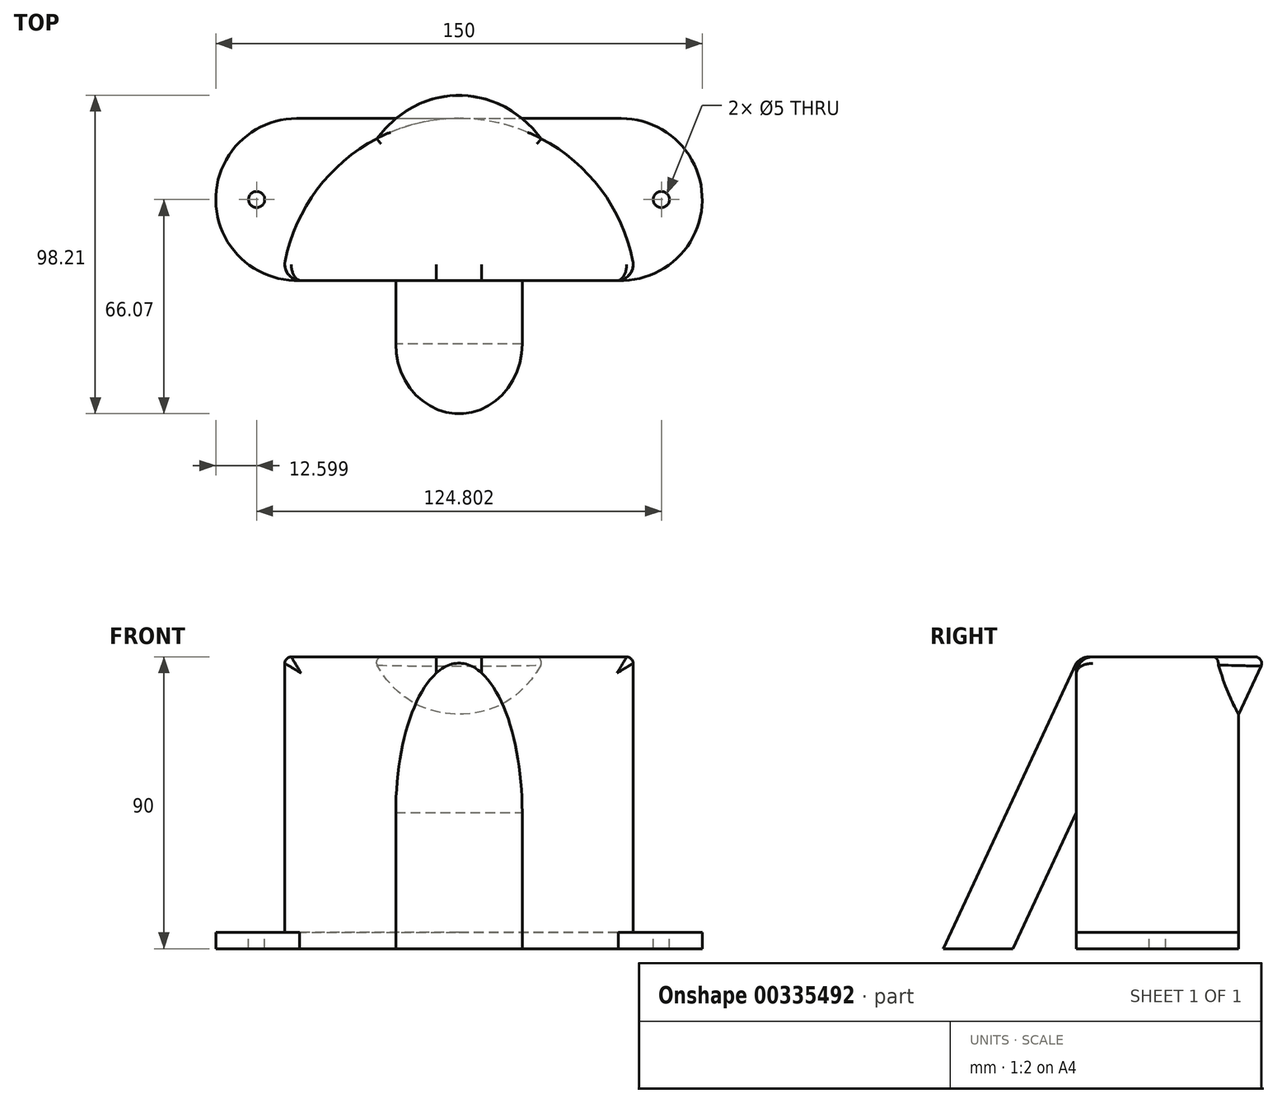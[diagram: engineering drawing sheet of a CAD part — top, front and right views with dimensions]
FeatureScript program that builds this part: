
annotation { "Feature Type Name" : "Feature", "Feature Type Description" : "" }
export const myFeature = defineFeature(function(context is Context, id is Id, definition is map)
    precondition{}
    {
        {
            var Q0;
            Q0=qCreatedBy(makeId("Top.planeOp"),FACE);
            var sketch = newSketch(context, id + "F0", { "sketchPlane" : qUnion([Q0])});
            skArc(sketch, "E0", {"start": v(50, 0) * mm, "mid": v(0, 50) * mm, "end": v(-50, 0) * mm});
            skLineSegment(sketch, "E1", {"start": v(-50, 0) * mm, "end": v(50, 0) * mm});
            skLineSegment(sketch, "E2", {"start": v(0, 50) * mm, "end": v(-50, 50) * mm});
            skLineSegment(sketch, "E3", {"start": v(0, 50) * mm, "end": v(50, 50) * mm});
            skArc(sketch, "E4", {"start": v(50, 0) * mm, "mid": v(75, 25) * mm, "end": v(50, 50) * mm});
            skArc(sketch, "E5", {"start": v(-50, 50) * mm, "mid": v(-75, 25) * mm, "end": v(-50, 0) * mm});
            skSolve(sketch);
        }
        {
            var Q0;
            Q0 = qSketchRegion(id + "F0", true);
            extrude(context, id + "F1", {"entities" : qUnion([Q0]), "depth" : 5 * mm});
        }
        {
            var Q0;
            Q0=makeQuery(id+"F1.opExtrude","CAP_FACE",FACE,{"disambiguationData":[OSD([sQuery(id+"F0.wireOp",EDGE,"E1"),sQuery(id+"F0.wireOp",EDGE,"E2"),sQuery(id+"F0.wireOp",EDGE,"E3"),sQuery(id+"F0.wireOp",EDGE,"E4"),sQuery(id+"F0.wireOp",EDGE,"E5")])],"isStart":false});
            var sketch = newSketch(context, id + "F2", { "sketchPlane" : qUnion([Q0])});
            skArc(sketch, "E6", {"start": v(54.47, 0) * mm, "mid": v(0, 50) * mm, "end": v(-54.47, 0) * mm});
            skLineSegment(sketch, "E7", {"start": v(-54.47, 0) * mm, "end": v(54.47, 0) * mm});
            skSolve(sketch);
        }
        {
            var Q0;
            Q0 = qSketchRegion(id + "F2", true);
            extrude(context, id + "F3", {"entities" : qUnion([Q0]), "operationType" : NewBodyOperationType.ADD, "depth" : 85 * mm});
        }
        {
            var Q0;
            Q0=makeQuery(id+"F3.opExtrude","CAP_EDGE",EDGE,{"disambiguationData":[OSD([sQuery(id+"F2.wireOp",EDGE,"E7")])],"isStart":false});
            cPlane(context, id + "F4", {"entities" : qUnion([Q0]), "cplaneType" : CPlaneType.LINE_ANGLE, "offset" : 25 * mm, "angle" : 65 * degree, "width" : 150 * mm, "height" : 150 * mm});
        }
        {
            var Q0;
            Q0=qCreatedBy(id+"F4.planeOp",FACE);
            var sketch = newSketch(context, id + "F5", { "sketchPlane" : qUnion([Q0])});
            skArc(sketch, "E8", {"start": v(32.5, -17.72) * mm, "mid": v(0, 14.78) * mm, "end": v(-32.5, -17.72) * mm});
            skLineSegment(sketch, "E9", {"start": v(-32.5, -17.72) * mm, "end": v(32.5, -17.72) * mm});
            skSolve(sketch);
        }
        {
            var Q0;
            {var subQ0=sQuery(id+"F5.wireOp",EDGE,"E9");Q0=makeQuery(id+"F5.imprint","IMPRINT",FACE,{"disambiguationData":[TD([[makeQuery(id+"F5.imprint","IMPRINT",EDGE,{"derivedFrom":subQ0}),1.0]])]});}
            var sketch = newSketch(context, id + "F6", { "sketchPlane" : qUnion([Q0])});
            skArc(sketch, "E10.0", {"start": v(-19.5, -17.72) * mm, "mid": v(0, -37.22) * mm, "end": v(19.5, -17.72) * mm});
            skLineSegment(sketch, "E11", {"start": v(-19.5, -17.72) * mm, "end": v(19.5, -17.72) * mm});
            skSolve(sketch);
        }
        {
            var Q0;
            Q0 = qSketchRegion(id + "F5", true);
            extrude(context, id + "F7", {"entities" : qUnion([Q0]), "operationType" : NewBodyOperationType.ADD, "endBound" : BoundingType.SYMMETRIC, "depth" : 73 * mm});
        }
        {
            var Q0;
            Q0 = qSketchRegion(id + "F6", true);
            extrude(context, id + "F8", {"entities" : qUnion([Q0]), "operationType" : NewBodyOperationType.ADD, "oppositeDirection" : true, "depth" : 111 * mm});
        }
        {
            var Q0;
            Q0=qCreatedBy(makeId("Right.planeOp"),FACE);
            var sketch = newSketch(context, id + "F9", { "sketchPlane" : qUnion([Q0])});
            skLineSegment(sketch, "E12.bottom", {"start": v(59.04, 0) * mm, "end": v(-73.98, 0) * mm});
            skLineSegment(sketch, "E12.top", {"start": v(59.04, -48.48) * mm, "end": v(-73.98, -48.48) * mm});
            skLineSegment(sketch, "E12.left", {"start": v(59.04, 0) * mm, "end": v(59.04, -48.48) * mm});
            skLineSegment(sketch, "E12.right", {"start": v(-73.98, 0) * mm, "end": v(-73.98, -48.48) * mm});
            skLineSegment(sketch, "E13.bottom", {"start": v(0, 90) * mm, "end": v(78.76, 90) * mm});
            skLineSegment(sketch, "E13.top", {"start": v(0, 126.33) * mm, "end": v(78.76, 126.33) * mm});
            skLineSegment(sketch, "E13.left", {"start": v(0, 90) * mm, "end": v(0, 126.33) * mm});
            skLineSegment(sketch, "E13.right", {"start": v(78.76, 90) * mm, "end": v(78.76, 126.33) * mm});
            skSolve(sketch);
        }
        {
            var Q0;
            Q0 = qSketchRegion(id + "F9", true);
            extrude(context, id + "F10", {"entities" : qUnion([Q0]), "operationType" : NewBodyOperationType.REMOVE, "endBound" : BoundingType.SYMMETRIC, "oppositeDirection" : true, "depth" : 300 * mm});
        }
        {
            var Q0;
            {var subQ0=sQuery(id+"F0.wireOp",EDGE,"E5");var subQ2=sQuery(id+"F0.wireOp",EDGE,"E3");var subQ3=sQuery(id+"F0.wireOp",EDGE,"E2");var subQ4=makeQuery(id+"F1.opExtrude","CAP_FACE",FACE,{"disambiguationData":[OSD([sQuery(id+"F0.wireOp",EDGE,"E1"),subQ3,subQ2,sQuery(id+"F0.wireOp",EDGE,"E4"),subQ0])],"isStart":false});Q0=makeQuery(id+"F3.boolean.opBoolean","SPLIT",FACE,{"disambiguationData":[TD([makeQuery(id+"F1.opExtrude","SWEPT_FACE",FACE,{"disambiguationData":[OSD([subQ0])]})])],"derivedFrom":subQ4});}
            var sketch = newSketch(context, id + "F11", { "sketchPlane" : qUnion([Q0])});
            skCircle(sketch, "E14", {"center": v(-62.4, 25) * mm, "radius": 2.5 * mm});
            skCircle(sketch, "E15", {"center": v(62.4, 25) * mm, "radius": 2.5 * mm});
            skSolve(sketch);
        }
        {
            var Q0;
            Q0 = qSketchRegion(id + "F11", true);
            extrude(context, id + "F12", {"entities" : qUnion([Q0]), "operationType" : NewBodyOperationType.REMOVE, "oppositeDirection" : true, "depth" : 25 * mm});
        }
        {
            var Q0;
            Q0=makeQuery(id+"F7.boolean.opBoolean","SPLIT",EDGE,{"disambiguationData":[OD(1.0)],"derivedFrom":makeQuery(id+"F3.opExtrude","CAP_EDGE",EDGE,{"disambiguationData":[OSD([sQuery(id+"F2.wireOp",EDGE,"E6")])],"isStart":false})});
            var Q1;
            Q1=makeQuery(id+"F10.boolean.opBoolean","INTERSECT",EDGE,{"derivedFrom":[makeQuery(id+"F7.opExtrude","SWEPT_FACE",FACE,{"disambiguationData":[OSD([sQuery(id+"F5.wireOp",EDGE,"E8")])]}),makeQuery(id+"F10.opExtrude","SWEPT_FACE",FACE,{"disambiguationData":[OSD([sQuery(id+"F9.wireOp",EDGE,"E13.bottom")])]})]});
            var Q2;
            Q2=makeQuery(id+"F7.boolean.opBoolean","SPLIT",EDGE,{"disambiguationData":[OD(0.0)],"derivedFrom":makeQuery(id+"F3.opExtrude","CAP_EDGE",EDGE,{"disambiguationData":[OSD([sQuery(id+"F2.wireOp",EDGE,"E6")])],"isStart":false})});
            fillet(context, id + "F13", {"entities" : qUnion([Q0, Q1, Q2]), "radius" : 2 * mm, "tangentPropagation" : true, "allowEdgeOverflow" : false});
        }
        {
            var Q0;
            {var subQ0=sQuery(id+"F2.wireOp",EDGE,"E7");var subQ1=sQuery(id+"F2.wireOp",EDGE,"E6");Q0=makeQuery(id+"F3.opExtrude","SWEPT_EDGE",EDGE,{"disambiguationData":[OSD([subQ1,subQ0]),TDD([makeQuery(id+"F2.imprint","INTERSECT",VERTEX,{"disambiguationData":[OD(0.0)],"derivedFrom":[subQ1,subQ0]})])]});}
            var Q1;
            {var subQ0=sQuery(id+"F2.wireOp",EDGE,"E7");var subQ1=sQuery(id+"F2.wireOp",EDGE,"E6");Q1=makeQuery(id+"F3.opExtrude","SWEPT_EDGE",EDGE,{"disambiguationData":[OSD([subQ1,subQ0]),TDD([makeQuery(id+"F2.imprint","INTERSECT",VERTEX,{"disambiguationData":[OD(1.0)],"derivedFrom":[subQ1,subQ0]})])]});}
            var Q2;
            Q2=makeQuery(id+"F3.opExtrude","CAP_EDGE",EDGE,{"disambiguationData":[OSD([sQuery(id+"F2.wireOp",EDGE,"E7")])],"isStart":false});
            fillet(context, id + "F14", {"entities" : qUnion([Q0, Q1, Q2]), "radius" : 5 * mm, "tangentPropagation" : true, "allowEdgeOverflow" : false});
        }
    });
